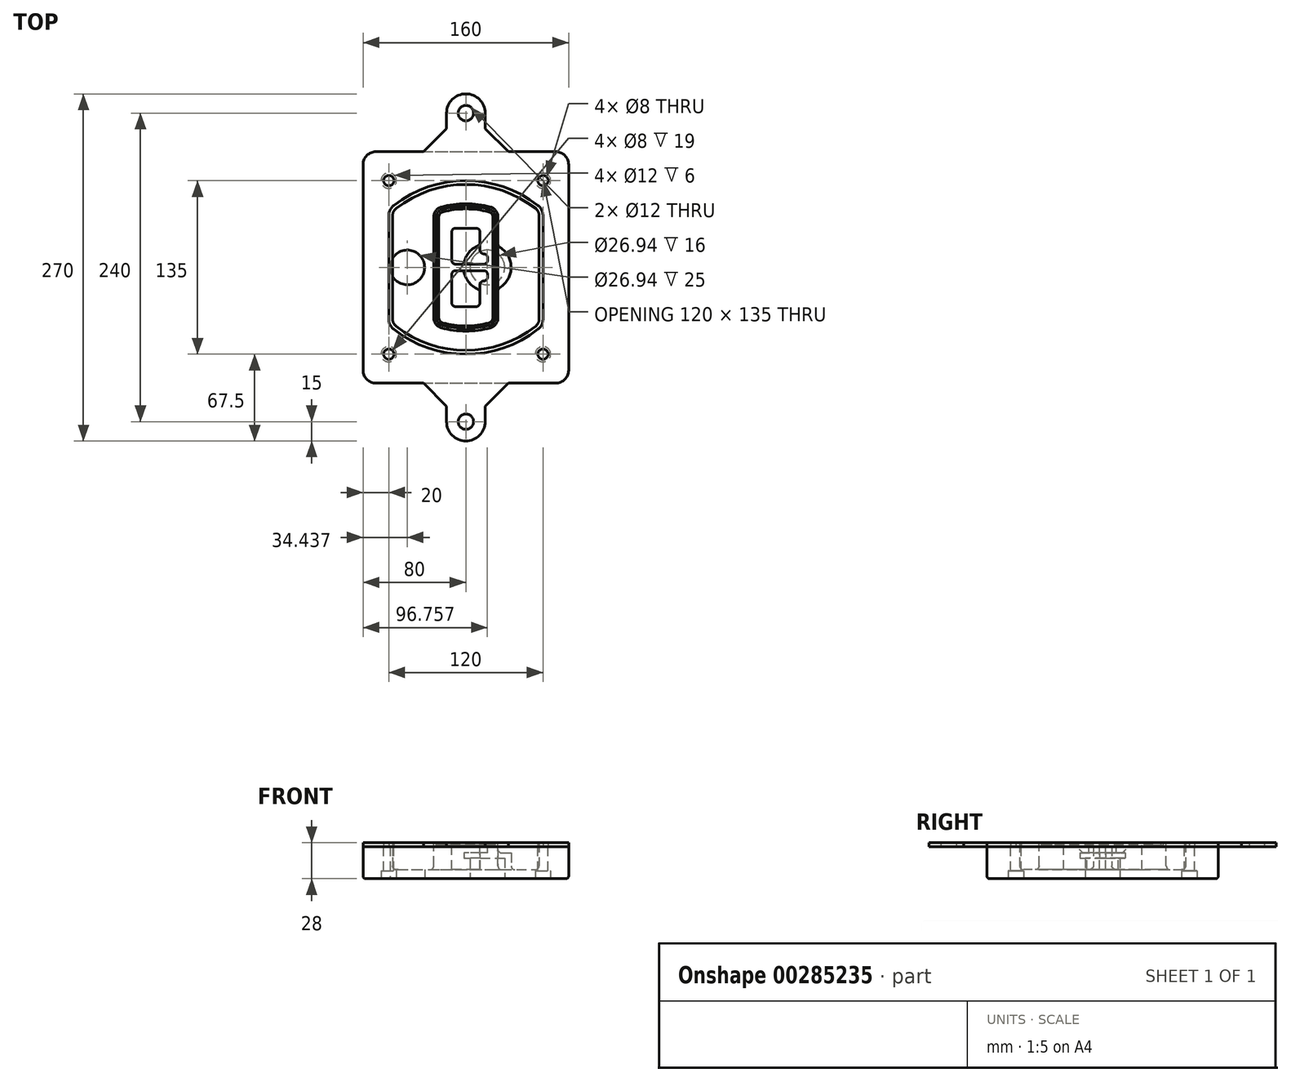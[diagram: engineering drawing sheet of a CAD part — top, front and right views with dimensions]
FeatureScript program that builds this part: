
annotation { "Feature Type Name" : "Feature", "Feature Type Description" : "" }
export const myFeature = defineFeature(function(context is Context, id is Id, definition is map)
    precondition{}
    {
        {
            var Q0;
            Q0=qCreatedBy(makeId("Top.planeOp"),FACE);
            var sketch = newSketch(context, id + "F0", { "sketchPlane" : qUnion([Q0])});
            skPoint(sketch, "E0.rect.middle", {"position": v(0, 0) * mm});
            skLineSegment(sketch, "E1.bottom", {"start": v(-70, -90) * mm, "end": v(70, -90) * mm});
            skLineSegment(sketch, "E1.top", {"start": v(-70, 90) * mm, "end": v(70, 90) * mm});
            skLineSegment(sketch, "E1.left", {"start": v(-80, -80) * mm, "end": v(-80, 80) * mm});
            skLineSegment(sketch, "E1.right", {"start": v(80, -80) * mm, "end": v(80, 80) * mm});
            skLineSegment(sketch, "E2", {"start": v(-80, 90) * mm, "end": v(80, -90) * mm, "construction": true});
            skLineSegment(sketch, "E3", {"start": v(80, 90) * mm, "end": v(-80, -90) * mm, "construction": true});
            skCircle(sketch, "E4", {"center": v(-60, 67.5) * mm, "radius": 4 * mm});
            skCircle(sketch, "E5", {"center": v(60, 67.5) * mm, "radius": 4 * mm});
            skCircle(sketch, "E6", {"center": v(60, -67.5) * mm, "radius": 4 * mm});
            skCircle(sketch, "E7", {"center": v(-60, -67.5) * mm, "radius": 4 * mm});
            skLineSegment(sketch, "E8", {"start": v(-60, 67.5) * mm, "end": v(60, 67.5) * mm, "construction": true});
            skLineSegment(sketch, "E9", {"start": v(60, 67.5) * mm, "end": v(60, -67.5) * mm, "construction": true});
            skLineSegment(sketch, "E10", {"start": v(60, -67.5) * mm, "end": v(-60, -67.5) * mm, "construction": true});
            skLineSegment(sketch, "E11", {"start": v(-60, -67.5) * mm, "end": v(-60, 67.5) * mm, "construction": true});
            skLineSegment(sketch, "E12", {"start": v(-60, 40.3) * mm, "end": v(-60, -40.3) * mm});
            skLineSegment(sketch, "E13", {"start": v(60, 40.3) * mm, "end": v(60, -40.3) * mm});
            skArc(sketch, "E14", {"start": v(56.15, 48.18) * mm, "mid": v(0, 67.5) * mm, "end": v(-56.15, 48.18) * mm});
            skArc(sketch, "E15", {"start": v(-56.15, -48.18) * mm, "mid": v(0, -67.5) * mm, "end": v(56.15, -48.18) * mm});
            skLineSegment(sketch, "E16", {"start": v(-60, 0) * mm, "end": v(60, 0) * mm, "construction": true});
            skPoint(sketch, "E17.visualSharp", {"position": v(-60, -45) * mm});
            skArc(sketch, "E17.filletArc", {"start": v(-60, -40.3) * mm, "mid": v(-58.99, -44.68) * mm, "end": v(-56.15, -48.18) * mm});
            skPoint(sketch, "E18.visualSharp", {"position": v(-60, 45) * mm});
            skArc(sketch, "E18.filletArc", {"start": v(-56.15, 48.18) * mm, "mid": v(-58.99, 44.68) * mm, "end": v(-60, 40.3) * mm});
            skPoint(sketch, "E19.visualSharp", {"position": v(60, 45) * mm});
            skArc(sketch, "E19.filletArc", {"start": v(60, 40.3) * mm, "mid": v(58.99, 44.68) * mm, "end": v(56.15, 48.18) * mm});
            skPoint(sketch, "E20.visualSharp", {"position": v(60, -45) * mm});
            skArc(sketch, "E20.filletArc", {"start": v(56.15, -48.18) * mm, "mid": v(58.99, -44.68) * mm, "end": v(60, -40.3) * mm});
            skPoint(sketch, "E21.visualSharp", {"position": v(-80, 90) * mm});
            skArc(sketch, "E21.filletArc", {"start": v(-70, 90) * mm, "mid": v(-77.07, 87.07) * mm, "end": v(-80, 80) * mm});
            skPoint(sketch, "E22.visualSharp", {"position": v(80, 90) * mm});
            skArc(sketch, "E22.filletArc", {"start": v(80, 80) * mm, "mid": v(77.07, 87.07) * mm, "end": v(70, 90) * mm});
            skPoint(sketch, "E23.visualSharp", {"position": v(80, -90) * mm});
            skArc(sketch, "E23.filletArc", {"start": v(70, -90) * mm, "mid": v(77.07, -87.07) * mm, "end": v(80, -80) * mm});
            skPoint(sketch, "E24.visualSharp", {"position": v(-80, -90) * mm});
            skArc(sketch, "E24.filletArc", {"start": v(-80, -80) * mm, "mid": v(-77.07, -87.07) * mm, "end": v(-70, -90) * mm});
            skArc(sketch, "E25.0", {"start": v(57, 40.3) * mm, "mid": v(56.3, 43.36) * mm, "end": v(54.3, 45.81) * mm});
            skLineSegment(sketch, "E25.1", {"start": v(57, 40.3) * mm, "end": v(57, -40.3) * mm});
            skArc(sketch, "E25.2", {"start": v(54.3, -45.81) * mm, "mid": v(56.3, -43.36) * mm, "end": v(57, -40.3) * mm});
            skArc(sketch, "E25.3", {"start": v(-54.3, -45.81) * mm, "mid": v(0, -64.5) * mm, "end": v(54.3, -45.81) * mm});
            skArc(sketch, "E25.4", {"start": v(-57, -40.3) * mm, "mid": v(-56.3, -43.36) * mm, "end": v(-54.3, -45.81) * mm});
            skArc(sketch, "E25.5", {"start": v(54.3, 45.81) * mm, "mid": v(0, 64.5) * mm, "end": v(-54.3, 45.81) * mm});
            skLineSegment(sketch, "E25.6", {"start": v(-57, 40.3) * mm, "end": v(-57, -40.3) * mm});
            skArc(sketch, "E25.7", {"start": v(-54.3, 45.81) * mm, "mid": v(-56.3, 43.36) * mm, "end": v(-57, 40.3) * mm});
            skArc(sketch, "E26.0", {"start": v(-58.62, 51.33) * mm, "mid": v(-62.58, 46.43) * mm, "end": v(-64, 40.3) * mm});
            skArc(sketch, "E26.1", {"start": v(58.62, 51.33) * mm, "mid": v(0, 71.5) * mm, "end": v(-58.62, 51.33) * mm});
            skArc(sketch, "E26.2", {"start": v(64, 40.3) * mm, "mid": v(62.58, 46.43) * mm, "end": v(58.62, 51.33) * mm});
            skLineSegment(sketch, "E26.3", {"start": v(64, 40.3) * mm, "end": v(64, -40.3) * mm});
            skArc(sketch, "E26.4", {"start": v(58.62, -51.33) * mm, "mid": v(62.58, -46.43) * mm, "end": v(64, -40.3) * mm});
            skLineSegment(sketch, "E26.5", {"start": v(-64, 40.3) * mm, "end": v(-64, -40.3) * mm});
            skArc(sketch, "E26.6", {"start": v(-58.62, -51.33) * mm, "mid": v(0, -71.5) * mm, "end": v(58.62, -51.33) * mm});
            skArc(sketch, "E26.7", {"start": v(-64, -40.3) * mm, "mid": v(-62.58, -46.43) * mm, "end": v(-58.62, -51.33) * mm});
            skSolve(sketch);
        }
        {
            var Q0;
            Q0=makeQuery(id+"F0.imprint","IMPRINT",FACE,{"disambiguationData":[TD([[makeQuery(id+"F0.imprint","IMPRINT",EDGE,{"derivedFrom":sQuery(id+"F0.wireOp",EDGE,"E1.bottom")}),1.0]])]});
            var Q1;
            Q1=makeQuery(id+"F0.imprint","IMPRINT",FACE,{"disambiguationData":[TD([[makeQuery(id+"F0.imprint","IMPRINT",EDGE,{"derivedFrom":sQuery(id+"F0.wireOp",EDGE,"E12")}),1.0]])]});
            var Q2;
            Q2=makeQuery(id+"F0.imprint","IMPRINT",FACE,{"disambiguationData":[TD([[makeQuery(id+"F0.imprint","IMPRINT",EDGE,{"derivedFrom":sQuery(id+"F0.wireOp",EDGE,"E25.0")}),1.0]])]});
            var Q3;
            Q3=makeQuery(id+"F0.imprint","IMPRINT",FACE,{"disambiguationData":[TD([[makeQuery(id+"F0.imprint","IMPRINT",EDGE,{"derivedFrom":sQuery(id+"F0.wireOp",EDGE,"E12")}),-1.0]])]});
            extrude(context, id + "F1", {"entities" : qUnion([Q0, Q1, Q2, Q3]), "oppositeDirection" : true, "depth" : 25 * mm});
        }
        {
            var Q0;
            Q0=makeQuery(id+"F0.imprint","IMPRINT",FACE,{"disambiguationData":[TD([[makeQuery(id+"F0.imprint","IMPRINT",EDGE,{"derivedFrom":sQuery(id+"F0.wireOp",EDGE,"E12")}),1.0]])]});
            extrude(context, id + "F2", {"entities" : qUnion([Q0]), "operationType" : NewBodyOperationType.ADD, "depth" : 3 * mm});
        }
        {
            var Q0;
            Q0=makeQuery(id+"F0.imprint","IMPRINT",FACE,{"disambiguationData":[TD([[makeQuery(id+"F0.imprint","IMPRINT",EDGE,{"derivedFrom":sQuery(id+"F0.wireOp",EDGE,"E25.0")}),1.0]])]});
            extrude(context, id + "F3", {"entities" : qUnion([Q0]), "operationType" : NewBodyOperationType.REMOVE, "oppositeDirection" : true, "depth" : 18 * mm});
        }
        {
            var Q0;
            Q0=makeQuery(id+"F2.opExtrude","CAP_FACE",FACE,{"disambiguationData":[OSD([sQuery(id+"F0.wireOp",EDGE,"E12"),sQuery(id+"F0.wireOp",EDGE,"E13"),sQuery(id+"F0.wireOp",EDGE,"E14"),sQuery(id+"F0.wireOp",EDGE,"E15"),sQuery(id+"F0.wireOp",EDGE,"E17.filletArc"),sQuery(id+"F0.wireOp",EDGE,"E18.filletArc"),sQuery(id+"F0.wireOp",EDGE,"E19.filletArc"),sQuery(id+"F0.wireOp",EDGE,"E20.filletArc"),sQuery(id+"F0.wireOp",EDGE,"E25.0"),sQuery(id+"F0.wireOp",EDGE,"E25.1"),sQuery(id+"F0.wireOp",EDGE,"E25.2"),sQuery(id+"F0.wireOp",EDGE,"E25.3"),sQuery(id+"F0.wireOp",EDGE,"E25.4"),sQuery(id+"F0.wireOp",EDGE,"E25.5"),sQuery(id+"F0.wireOp",EDGE,"E25.6"),sQuery(id+"F0.wireOp",EDGE,"E25.7")])],"isStart":false});
            var sketch = newSketch(context, id + "F4", { "sketchPlane" : qUnion([Q0])});
            skArc(sketch, "E27.0", {"start": v(-19.08, -46.97) * mm, "mid": v(0, -49.5) * mm, "end": v(19.08, -46.97) * mm});
            skArc(sketch, "E28.0", {"start": v(19.08, 46.97) * mm, "mid": v(0, 49.5) * mm, "end": v(-19.08, 46.97) * mm});
            skLineSegment(sketch, "E29", {"start": v(-25, 39.25) * mm, "end": v(-25, -39.25) * mm});
            skLineSegment(sketch, "E30", {"start": v(25, 39.25) * mm, "end": v(25, -39.25) * mm});
            skLineSegment(sketch, "E31", {"start": v(-25, 45.1) * mm, "end": v(25, 45.1) * mm, "construction": true});
            skLineSegment(sketch, "E32", {"start": v(-25, -45.1) * mm, "end": v(25, -45.1) * mm, "construction": true});
            skPoint(sketch, "E33.visualSharp", {"position": v(-25, 45.1) * mm});
            skArc(sketch, "E33.filletArc", {"start": v(-19.08, 46.97) * mm, "mid": v(-23.35, 44.11) * mm, "end": v(-25, 39.25) * mm});
            skPoint(sketch, "E34.visualSharp", {"position": v(25, 45.1) * mm});
            skArc(sketch, "E34.filletArc", {"start": v(25, 39.25) * mm, "mid": v(23.35, 44.11) * mm, "end": v(19.08, 46.97) * mm});
            skPoint(sketch, "E35.visualSharp", {"position": v(25, -45.1) * mm});
            skArc(sketch, "E35.filletArc", {"start": v(19.08, -46.97) * mm, "mid": v(23.35, -44.11) * mm, "end": v(25, -39.25) * mm});
            skPoint(sketch, "E36.visualSharp", {"position": v(-25, -45.1) * mm});
            skArc(sketch, "E36.filletArc", {"start": v(-25, -39.25) * mm, "mid": v(-23.35, -44.11) * mm, "end": v(-19.08, -46.97) * mm});
            skArc(sketch, "E37.0", {"start": v(54.3, 45.81) * mm, "mid": v(0, 64.5) * mm, "end": v(-54.3, 45.81) * mm});
            skArc(sketch, "E37.1", {"start": v(-54.3, 45.81) * mm, "mid": v(-56.3, 43.36) * mm, "end": v(-57, 40.3) * mm});
            skLineSegment(sketch, "E37.2", {"start": v(-57, 40.3) * mm, "end": v(-57, -40.3) * mm});
            skArc(sketch, "E37.3", {"start": v(-57, -40.3) * mm, "mid": v(-56.3, -43.36) * mm, "end": v(-54.3, -45.81) * mm});
            skArc(sketch, "E37.4", {"start": v(-54.3, -45.81) * mm, "mid": v(0, -64.5) * mm, "end": v(54.3, -45.81) * mm});
            skArc(sketch, "E37.5", {"start": v(54.3, -45.81) * mm, "mid": v(56.3, -43.36) * mm, "end": v(57, -40.3) * mm});
            skLineSegment(sketch, "E37.6", {"start": v(57, 40.3) * mm, "end": v(57, -40.3) * mm});
            skArc(sketch, "E37.7", {"start": v(57, 40.3) * mm, "mid": v(56.3, 43.36) * mm, "end": v(54.3, 45.81) * mm});
            skLineSegment(sketch, "E38.0", {"start": v(23, 39.25) * mm, "end": v(23, -39.25) * mm});
            skArc(sketch, "E38.1", {"start": v(18.56, -45.04) * mm, "mid": v(21.76, -42.9) * mm, "end": v(23, -39.25) * mm});
            skArc(sketch, "E38.2", {"start": v(-18.56, -45.04) * mm, "mid": v(0, -47.5) * mm, "end": v(18.56, -45.04) * mm});
            skArc(sketch, "E38.3", {"start": v(-23, -39.25) * mm, "mid": v(-21.76, -42.9) * mm, "end": v(-18.56, -45.04) * mm});
            skLineSegment(sketch, "E38.4", {"start": v(-23, 39.25) * mm, "end": v(-23, -39.25) * mm});
            skArc(sketch, "E38.5", {"start": v(23, 39.25) * mm, "mid": v(21.76, 42.9) * mm, "end": v(18.56, 45.04) * mm});
            skArc(sketch, "E38.6", {"start": v(-18.56, 45.04) * mm, "mid": v(-21.76, 42.9) * mm, "end": v(-23, 39.25) * mm});
            skArc(sketch, "E38.7", {"start": v(18.56, 45.04) * mm, "mid": v(0, 47.5) * mm, "end": v(-18.56, 45.04) * mm});
            skArc(sketch, "E39.0", {"start": v(21, 39.25) * mm, "mid": v(20.18, 41.68) * mm, "end": v(18.04, 43.1) * mm});
            skLineSegment(sketch, "E39.1", {"start": v(21, 39.25) * mm, "end": v(21, -39.25) * mm});
            skArc(sketch, "E39.2", {"start": v(18.04, -43.1) * mm, "mid": v(20.18, -41.68) * mm, "end": v(21, -39.25) * mm});
            skArc(sketch, "E39.3", {"start": v(-18.04, -43.1) * mm, "mid": v(0, -45.5) * mm, "end": v(18.04, -43.1) * mm});
            skArc(sketch, "E39.4", {"start": v(-21, -39.25) * mm, "mid": v(-20.18, -41.68) * mm, "end": v(-18.04, -43.1) * mm});
            skArc(sketch, "E39.5", {"start": v(18.04, 43.1) * mm, "mid": v(0, 45.5) * mm, "end": v(-18.04, 43.1) * mm});
            skLineSegment(sketch, "E39.6", {"start": v(-21, 39.25) * mm, "end": v(-21, -39.25) * mm});
            skArc(sketch, "E39.7", {"start": v(-18.04, 43.1) * mm, "mid": v(-20.18, 41.68) * mm, "end": v(-21, 39.25) * mm});
            skLineSegment(sketch, "E40", {"start": v(-25, 0) * mm, "end": v(25, 0) * mm, "construction": true});
            skLineSegment(sketch, "E41", {"start": v(-11, 5.5) * mm, "end": v(-11, 27.5) * mm});
            skLineSegment(sketch, "E42", {"start": v(-8, 30.5) * mm, "end": v(8, 30.5) * mm});
            skLineSegment(sketch, "E43", {"start": v(11, 27.5) * mm, "end": v(11, 13.5) * mm});
            skLineSegment(sketch, "E44", {"start": v(14, 10.5) * mm, "end": v(14, 10.5) * mm});
            skLineSegment(sketch, "E45", {"start": v(17, 7.5) * mm, "end": v(17, 5.5) * mm});
            skLineSegment(sketch, "E46", {"start": v(14, 2.5) * mm, "end": v(-8, 2.5) * mm});
            skPoint(sketch, "E47.visualSharp", {"position": v(-11, 30.5) * mm});
            skArc(sketch, "E47.filletArc", {"start": v(-8, 30.5) * mm, "mid": v(-10.12, 29.62) * mm, "end": v(-11, 27.5) * mm});
            skPoint(sketch, "E48.visualSharp", {"position": v(11, 30.5) * mm});
            skArc(sketch, "E48.filletArc", {"start": v(11, 27.5) * mm, "mid": v(10.12, 29.62) * mm, "end": v(8, 30.5) * mm});
            skPoint(sketch, "E49.visualSharp", {"position": v(11, 10.5) * mm});
            skArc(sketch, "E49.filletArc", {"start": v(11, 13.5) * mm, "mid": v(11.88, 11.38) * mm, "end": v(14, 10.5) * mm});
            skPoint(sketch, "E50.visualSharp", {"position": v(17, 10.5) * mm});
            skArc(sketch, "E50.filletArc", {"start": v(17, 7.5) * mm, "mid": v(16.12, 9.62) * mm, "end": v(14, 10.5) * mm});
            skPoint(sketch, "E51.visualSharp", {"position": v(17, 2.5) * mm});
            skArc(sketch, "E51.filletArc", {"start": v(14, 2.5) * mm, "mid": v(16.12, 3.38) * mm, "end": v(17, 5.5) * mm});
            skPoint(sketch, "E52.visualSharp", {"position": v(-11, 2.5) * mm});
            skArc(sketch, "E52.filletArc", {"start": v(-11, 5.5) * mm, "mid": v(-10.12, 3.38) * mm, "end": v(-8, 2.5) * mm});
            skLineSegment(sketch, "E53.0.MirrorCS", {"start": v(14, -2.5) * mm, "end": v(-8, -2.5) * mm});
            skArc(sketch, "E54.0.MirrorCS", {"start": v(-11, -5.5) * mm, "mid": v(-10.12, -3.38) * mm, "end": v(-8, -2.5) * mm});
            skLineSegment(sketch, "E55.0.MirrorCS", {"start": v(-11, -5.5) * mm, "end": v(-11, -27.5) * mm});
            skArc(sketch, "E56.0.MirrorCS", {"start": v(-8, -30.5) * mm, "mid": v(-10.12, -29.62) * mm, "end": v(-11, -27.5) * mm});
            skLineSegment(sketch, "E57.0.MirrorCS", {"start": v(-8, -30.5) * mm, "end": v(8, -30.5) * mm});
            skArc(sketch, "E58.0.MirrorCS", {"start": v(11, -27.5) * mm, "mid": v(10.12, -29.62) * mm, "end": v(8, -30.5) * mm});
            skLineSegment(sketch, "E59.0.MirrorCS", {"start": v(11, -27.5) * mm, "end": v(11, -13.5) * mm});
            skArc(sketch, "E60.0.MirrorCS", {"start": v(11, -13.5) * mm, "mid": v(11.88, -11.38) * mm, "end": v(14, -10.5) * mm});
            skArc(sketch, "E61.0.MirrorCS", {"start": v(17, -7.5) * mm, "mid": v(16.12, -9.62) * mm, "end": v(14, -10.5) * mm});
            skLineSegment(sketch, "E62.0.MirrorCS", {"start": v(17, -7.5) * mm, "end": v(17, -5.5) * mm});
            skArc(sketch, "E63.0.MirrorCS", {"start": v(14, -2.5) * mm, "mid": v(16.12, -3.38) * mm, "end": v(17, -5.5) * mm});
            skSolve(sketch);
        }
        {
            var Q0;
            Q0=makeQuery(id+"F4.imprint","IMPRINT",FACE,{"disambiguationData":[TD([[makeQuery(id+"F4.imprint","IMPRINT",EDGE,{"derivedFrom":sQuery(id+"F4.wireOp",EDGE,"E27.0")}),1.0]])]});
            var Q1;
            Q1=makeQuery(id+"F4.imprint","IMPRINT",FACE,{"disambiguationData":[TD([[makeQuery(id+"F4.imprint","IMPRINT",EDGE,{"derivedFrom":sQuery(id+"F4.wireOp",EDGE,"E38.0")}),-1.0]])]});
            var Q2;
            Q2=makeQuery(id+"F4.imprint","IMPRINT",FACE,{"disambiguationData":[TD([[makeQuery(id+"F4.imprint","IMPRINT",EDGE,{"derivedFrom":sQuery(id+"F4.wireOp",EDGE,"E39.0")}),1.0]])]});
            extrude(context, id + "F5", {"entities" : qUnion([Q0, Q1, Q2]), "operationType" : NewBodyOperationType.ADD, "endBound" : BoundingType.UP_TO_NEXT, "oppositeDirection" : true, "depth" : 25 * mm});
        }
        {
            var Q0;
            Q0=makeQuery(id+"F4.imprint","IMPRINT",FACE,{"disambiguationData":[TD([[makeQuery(id+"F4.imprint","IMPRINT",EDGE,{"derivedFrom":sQuery(id+"F4.wireOp",EDGE,"E38.0")}),-1.0]])]});
            extrude(context, id + "F6", {"entities" : qUnion([Q0]), "operationType" : NewBodyOperationType.REMOVE, "oppositeDirection" : true, "depth" : 2 * mm});
        }
        {
            var Q0;
            Q0=makeQuery(id+"F1.opExtrude","CAP_FACE",FACE,{"disambiguationData":[OSD([sQuery(id+"F0.wireOp",EDGE,"E1.bottom"),sQuery(id+"F0.wireOp",EDGE,"E1.top"),sQuery(id+"F0.wireOp",EDGE,"E1.left"),sQuery(id+"F0.wireOp",EDGE,"E1.right"),sQuery(id+"F0.wireOp",EDGE,"E4"),sQuery(id+"F0.wireOp",EDGE,"E5"),sQuery(id+"F0.wireOp",EDGE,"E6"),sQuery(id+"F0.wireOp",EDGE,"E7"),sQuery(id+"F0.wireOp",EDGE,"E21.filletArc"),sQuery(id+"F0.wireOp",EDGE,"E22.filletArc"),sQuery(id+"F0.wireOp",EDGE,"E23.filletArc"),sQuery(id+"F0.wireOp",EDGE,"E24.filletArc")])],"isStart":false});
            var sketch = newSketch(context, id + "F7", { "sketchPlane" : qUnion([Q0])});
            skCircle(sketch, "E64", {"center": v(16.76, 0) * mm, "radius": 13.47 * mm});
            skCircle(sketch, "E65", {"center": v(-45.56, 0) * mm, "radius": 13.47 * mm});
            skLineSegment(sketch, "E66", {"start": v(80, 0) * mm, "end": v(-80, 0) * mm});
            skCircle(sketch, "E67", {"center": v(16.76, 0) * mm, "radius": 18.47 * mm});
            skCircle(sketch, "E68", {"center": v(60, -67.5) * mm, "radius": 6 * mm});
            skCircle(sketch, "E69", {"center": v(-60, -67.5) * mm, "radius": 6 * mm});
            skCircle(sketch, "E70", {"center": v(-60, 67.5) * mm, "radius": 6 * mm});
            skCircle(sketch, "E71", {"center": v(60, 67.5) * mm, "radius": 6 * mm});
            skSolve(sketch);
        }
        {
            var Q0;
            {var subQ1=sQuery(id+"F7.wireOp",EDGE,"E66");var subQ4=sQuery(id+"F7.wireOp",EDGE,"E64");var subQ6=makeQuery(id+"F7.imprint","INTERSECT",VERTEX,{"disambiguationData":[OD(0.0)],"derivedFrom":[subQ4,subQ1]});Q0=makeQuery(id+"F7.imprint","IMPRINT",FACE,{"disambiguationData":[TD([[makeQuery(id+"F7.imprint","IMPRINT",EDGE,{"disambiguationData":[TD([[subQ6,-1.0]])],"derivedFrom":subQ4}),-1.0]])]});}
            var Q1;
            {var subQ0=sQuery(id+"F7.wireOp",EDGE,"E66");var subQ1=sQuery(id+"F7.wireOp",EDGE,"E64");var subQ3=makeQuery(id+"F7.imprint","INTERSECT",VERTEX,{"disambiguationData":[OD(0.0)],"derivedFrom":[subQ1,subQ0]});Q1=makeQuery(id+"F7.imprint","IMPRINT",FACE,{"disambiguationData":[TD([[makeQuery(id+"F7.imprint","IMPRINT",EDGE,{"disambiguationData":[TD([[subQ3,-1.0]])],"derivedFrom":subQ1}),1.0]])]});}
            var Q2;
            {var subQ0=sQuery(id+"F7.wireOp",EDGE,"E66");var subQ1=sQuery(id+"F7.wireOp",EDGE,"E64");var subQ3=makeQuery(id+"F7.imprint","INTERSECT",VERTEX,{"disambiguationData":[OD(0.0)],"derivedFrom":[subQ1,subQ0]});Q2=makeQuery(id+"F7.imprint","IMPRINT",FACE,{"disambiguationData":[TD([[makeQuery(id+"F7.imprint","IMPRINT",EDGE,{"disambiguationData":[TD([[subQ3,1.0]])],"derivedFrom":subQ1}),1.0]])]});}
            var Q3;
            {var subQ1=sQuery(id+"F7.wireOp",EDGE,"E66");var subQ4=sQuery(id+"F7.wireOp",EDGE,"E64");var subQ6=makeQuery(id+"F7.imprint","INTERSECT",VERTEX,{"disambiguationData":[OD(0.0)],"derivedFrom":[subQ4,subQ1]});Q3=makeQuery(id+"F7.imprint","IMPRINT",FACE,{"disambiguationData":[TD([[makeQuery(id+"F7.imprint","IMPRINT",EDGE,{"disambiguationData":[TD([[subQ6,1.0]])],"derivedFrom":subQ4}),-1.0]])]});}
            extrude(context, id + "F8", {"entities" : qUnion([Q0, Q1, Q2, Q3]), "operationType" : NewBodyOperationType.ADD, "oppositeDirection" : true, "depth" : 20 * mm});
        }
        {
            var Q0;
            {var subQ0=sQuery(id+"F7.wireOp",EDGE,"E66");var subQ1=sQuery(id+"F7.wireOp",EDGE,"E64");var subQ3=makeQuery(id+"F7.imprint","INTERSECT",VERTEX,{"disambiguationData":[OD(0.0)],"derivedFrom":[subQ1,subQ0]});Q0=makeQuery(id+"F7.imprint","IMPRINT",FACE,{"disambiguationData":[TD([[makeQuery(id+"F7.imprint","IMPRINT",EDGE,{"disambiguationData":[TD([[subQ3,-1.0]])],"derivedFrom":subQ1}),1.0]])]});}
            var Q1;
            {var subQ0=sQuery(id+"F7.wireOp",EDGE,"E66");var subQ1=sQuery(id+"F7.wireOp",EDGE,"E64");var subQ3=makeQuery(id+"F7.imprint","INTERSECT",VERTEX,{"disambiguationData":[OD(0.0)],"derivedFrom":[subQ1,subQ0]});Q1=makeQuery(id+"F7.imprint","IMPRINT",FACE,{"disambiguationData":[TD([[makeQuery(id+"F7.imprint","IMPRINT",EDGE,{"disambiguationData":[TD([[subQ3,1.0]])],"derivedFrom":subQ1}),1.0]])]});}
            extrude(context, id + "F9", {"entities" : qUnion([Q0, Q1]), "operationType" : NewBodyOperationType.REMOVE, "oppositeDirection" : true, "depth" : 16 * mm});
        }
        {
            var Q0;
            {var subQ0=sQuery(id+"F7.wireOp",EDGE,"E66");var subQ1=sQuery(id+"F7.wireOp",EDGE,"E65");var subQ3=makeQuery(id+"F7.imprint","INTERSECT",VERTEX,{"disambiguationData":[OD(0.0)],"derivedFrom":[subQ1,subQ0]});Q0=makeQuery(id+"F7.imprint","IMPRINT",FACE,{"disambiguationData":[TD([[makeQuery(id+"F7.imprint","IMPRINT",EDGE,{"disambiguationData":[TD([[subQ3,-1.0]])],"derivedFrom":subQ1}),1.0]])]});}
            var Q1;
            {var subQ0=sQuery(id+"F7.wireOp",EDGE,"E66");var subQ1=sQuery(id+"F7.wireOp",EDGE,"E65");var subQ3=makeQuery(id+"F7.imprint","INTERSECT",VERTEX,{"disambiguationData":[OD(0.0)],"derivedFrom":[subQ1,subQ0]});Q1=makeQuery(id+"F7.imprint","IMPRINT",FACE,{"disambiguationData":[TD([[makeQuery(id+"F7.imprint","IMPRINT",EDGE,{"disambiguationData":[TD([[subQ3,1.0]])],"derivedFrom":subQ1}),1.0]])]});}
            extrude(context, id + "F10", {"entities" : qUnion([Q0, Q1]), "operationType" : NewBodyOperationType.REMOVE, "oppositeDirection" : true, "depth" : 25 * mm});
        }
        {
            var Q0;
            Q0=makeQuery(id+"F7.imprint","IMPRINT",FACE,{"disambiguationData":[TD([[makeQuery(id+"F7.imprint","IMPRINT",EDGE,{"derivedFrom":sQuery(id+"F7.wireOp",EDGE,"E68")}),1.0]])]});
            var Q1;
            Q1=makeQuery(id+"F7.imprint","IMPRINT",FACE,{"disambiguationData":[TD([[makeQuery(id+"F7.imprint","IMPRINT",EDGE,{"derivedFrom":makeQuery(id+"F1.opExtrude","CAP_EDGE",EDGE,{"disambiguationData":[OSD([sQuery(id+"F0.wireOp",EDGE,"E5")])],"isStart":false})}),-1.0]])]});
            var Q2;
            Q2=makeQuery(id+"F7.imprint","IMPRINT",FACE,{"disambiguationData":[TD([[makeQuery(id+"F7.imprint","IMPRINT",EDGE,{"derivedFrom":sQuery(id+"F7.wireOp",EDGE,"E69")}),1.0]])]});
            var Q3;
            Q3=makeQuery(id+"F7.imprint","IMPRINT",FACE,{"disambiguationData":[TD([[makeQuery(id+"F7.imprint","IMPRINT",EDGE,{"derivedFrom":makeQuery(id+"F1.opExtrude","CAP_EDGE",EDGE,{"disambiguationData":[OSD([sQuery(id+"F0.wireOp",EDGE,"E4")])],"isStart":false})}),-1.0]])]});
            var Q4;
            Q4=makeQuery(id+"F7.imprint","IMPRINT",FACE,{"disambiguationData":[TD([[makeQuery(id+"F7.imprint","IMPRINT",EDGE,{"derivedFrom":sQuery(id+"F7.wireOp",EDGE,"E70")}),1.0]])]});
            var Q5;
            Q5=makeQuery(id+"F7.imprint","IMPRINT",FACE,{"disambiguationData":[TD([[makeQuery(id+"F7.imprint","IMPRINT",EDGE,{"derivedFrom":makeQuery(id+"F1.opExtrude","CAP_EDGE",EDGE,{"disambiguationData":[OSD([sQuery(id+"F0.wireOp",EDGE,"E7")])],"isStart":false})}),-1.0]])]});
            var Q6;
            Q6=makeQuery(id+"F7.imprint","IMPRINT",FACE,{"disambiguationData":[TD([[makeQuery(id+"F7.imprint","IMPRINT",EDGE,{"derivedFrom":sQuery(id+"F7.wireOp",EDGE,"E71")}),1.0]])]});
            var Q7;
            Q7=makeQuery(id+"F7.imprint","IMPRINT",FACE,{"disambiguationData":[TD([[makeQuery(id+"F7.imprint","IMPRINT",EDGE,{"derivedFrom":makeQuery(id+"F1.opExtrude","CAP_EDGE",EDGE,{"disambiguationData":[OSD([sQuery(id+"F0.wireOp",EDGE,"E6")])],"isStart":false})}),-1.0]])]});
            extrude(context, id + "F11", {"entities" : qUnion([Q0, Q1, Q2, Q3, Q4, Q5, Q6, Q7]), "operationType" : NewBodyOperationType.REMOVE, "oppositeDirection" : true, "depth" : 6 * mm});
        }
        {
            var Q0;
            Q0=makeQuery(id+"F9.boolean.opBoolean","COPY",FACE,{"derivedFrom":makeQuery(id+"F9.opExtrude","CAP_FACE",FACE,{"disambiguationData":[OSD([sQuery(id+"F7.wireOp",EDGE,"E64")])],"isStart":false})});
            var sketch = newSketch(context, id + "F12", { "sketchPlane" : qUnion([Q0])});
            skArc(sketch, "E72.0", {"start": v(11, 17.55) * mm, "mid": v(2.57, 11.82) * mm, "end": v(-1.54, 2.5) * mm});
            skArc(sketch, "E72.1", {"start": v(-1.54, -2.5) * mm, "mid": v(2.57, -11.82) * mm, "end": v(11, -17.55) * mm});
            skLineSegment(sketch, "E73", {"start": v(-1.54, -2.5) * mm, "end": v(14, -2.5) * mm});
            skLineSegment(sketch, "E74.0", {"start": v(14, 2.5) * mm, "end": v(-1.54, 2.5) * mm});
            skArc(sketch, "E74.1", {"start": v(14, 2.5) * mm, "mid": v(16.12, 3.38) * mm, "end": v(17, 5.5) * mm});
            skLineSegment(sketch, "E74.2", {"start": v(17, 7.5) * mm, "end": v(17, 5.5) * mm});
            skArc(sketch, "E74.3", {"start": v(17, 7.5) * mm, "mid": v(16.12, 9.62) * mm, "end": v(14, 10.5) * mm});
            skArc(sketch, "E74.4", {"start": v(11, 13.5) * mm, "mid": v(11.88, 11.38) * mm, "end": v(14, 10.5) * mm});
            skLineSegment(sketch, "E74.5", {"start": v(11, 17.55) * mm, "end": v(11, 13.5) * mm});
            skLineSegment(sketch, "E74.7", {"start": v(14, -2.5) * mm, "end": v(-1.54, -2.5) * mm});
            skArc(sketch, "E74.8", {"start": v(14, -2.5) * mm, "mid": v(16.12, -3.38) * mm, "end": v(17, -5.5) * mm});
            skLineSegment(sketch, "E74.9", {"start": v(17, -7.5) * mm, "end": v(17, -5.5) * mm});
            skArc(sketch, "E74.10", {"start": v(17, -7.5) * mm, "mid": v(16.12, -9.62) * mm, "end": v(14, -10.5) * mm});
            skArc(sketch, "E74.11", {"start": v(11, -13.5) * mm, "mid": v(11.88, -11.38) * mm, "end": v(14, -10.5) * mm});
            skLineSegment(sketch, "E74.12", {"start": v(11, -17.55) * mm, "end": v(11, -13.5) * mm});
            skPoint(sketch, "E75.orphan", {"position": v(11, -27.5) * mm});
            skPoint(sketch, "E76.orphan", {"position": v(-8, -2.5) * mm});
            skPoint(sketch, "E77.orphan", {"position": v(-8, 2.5) * mm});
            skPoint(sketch, "E78.orphan", {"position": v(11, 27.5) * mm});
            skSolve(sketch);
        }
        {
            var Q0;
            {var subQ7=sQuery(id+"F12.wireOp",EDGE,"E72.0");var subQ14=sQuery(id+"F12.wireOp",EDGE,"E72.1");var subQ16=sQuery(id+"F12.wireOp",EDGE,"E74.1");var subQ18=sQuery(id+"F12.wireOp",EDGE,"E74.8");Q0=qUnion([makeQuery(id+"F12.imprint","IMPRINT",FACE,{"disambiguationData":[TD([[makeQuery(id+"F12.imprint","IMPRINT",EDGE,{"derivedFrom":subQ7}),1.0]])]}),makeQuery(id+"F12.imprint","IMPRINT",FACE,{"disambiguationData":[TD([[makeQuery(id+"F12.imprint","IMPRINT",EDGE,{"derivedFrom":subQ14}),1.0]])]}),makeQuery(id+"F12.imprint","IMPRINT",FACE,{"disambiguationData":[TD([[makeQuery(id+"F12.imprint","IMPRINT",EDGE,{"derivedFrom":subQ16}),1.0]])]}),makeQuery(id+"F12.imprint","IMPRINT",FACE,{"disambiguationData":[TD([[makeQuery(id+"F12.imprint","IMPRINT",EDGE,{"derivedFrom":subQ18}),-1.0]])]})]);}
            var Q1;
            Q1=makeQuery(id+"F5.boolean.opBoolean","SPLIT",FACE,{"disambiguationData":[TD([makeQuery(id+"F5.opExtrude","SWEPT_FACE",FACE,{"disambiguationData":[OSD([sQuery(id+"F4.wireOp",EDGE,"E41")])]})])],"derivedFrom":makeQuery(id+"F3.boolean.opBoolean","COPY",FACE,{"derivedFrom":makeQuery(id+"F3.opExtrude","CAP_FACE",FACE,{"disambiguationData":[OSD([sQuery(id+"F0.wireOp",EDGE,"E25.0"),sQuery(id+"F0.wireOp",EDGE,"E25.1"),sQuery(id+"F0.wireOp",EDGE,"E25.2"),sQuery(id+"F0.wireOp",EDGE,"E25.3"),sQuery(id+"F0.wireOp",EDGE,"E25.4"),sQuery(id+"F0.wireOp",EDGE,"E25.5"),sQuery(id+"F0.wireOp",EDGE,"E25.6"),sQuery(id+"F0.wireOp",EDGE,"E25.7")])],"isStart":false})})});
            extrude(context, id + "F13", {"entities" : qUnion([Q0]), "operationType" : NewBodyOperationType.REMOVE, "endBound" : BoundingType.UP_TO_SURFACE, "endBoundEntityFace" : qUnion([Q1]), "depth" : 25 * mm});
        }
        {
            var Q0;
            Q0=makeQuery(id+"F3.boolean.opBoolean","COPY",EDGE,{"derivedFrom":makeQuery(id+"F3.opExtrude","CAP_EDGE",EDGE,{"disambiguationData":[OSD([sQuery(id+"F0.wireOp",EDGE,"E25.6")])],"isStart":false})});
            var Q1;
            Q1=makeQuery(id+"F8.boolean.opBoolean","INTERSECT",EDGE,{"derivedFrom":[makeQuery(id+"F5.opExtrude","SWEPT_FACE",FACE,{"disambiguationData":[OSD([sQuery(id+"F4.wireOp",EDGE,"E30")])]}),makeQuery(id+"F8.opExtrude","CAP_FACE",FACE,{"disambiguationData":[OSD([sQuery(id+"F7.wireOp",EDGE,"E67")])],"isStart":false})]});
            var Q2;
            Q2=makeQuery(id+"F8.boolean.opBoolean","INTERSECT",EDGE,{"disambiguationData":[OD(1.0)],"derivedFrom":[makeQuery(id+"F5.opExtrude","SWEPT_FACE",FACE,{"disambiguationData":[OSD([sQuery(id+"F4.wireOp",EDGE,"E30")])]}),makeQuery(id+"F8.opExtrude","SWEPT_FACE",FACE,{"disambiguationData":[OSD([sQuery(id+"F7.wireOp",EDGE,"E67")])]})]});
            var Q3;
            {var subQ0=sQuery(id+"F4.wireOp",EDGE,"E30");Q3=makeQuery(id+"F8.boolean.opBoolean","SPLIT",EDGE,{"disambiguationData":[TD([makeQuery(id+"F5.opExtrude","SWEPT_FACE",FACE,{"disambiguationData":[OSD([sQuery(id+"F4.wireOp",EDGE,"E35.filletArc")])]})])],"derivedFrom":makeQuery(id+"F5.opExtrude","CAP_EDGE",EDGE,{"disambiguationData":[OSD([subQ0])],"isStart":false})});}
            var Q4;
            {var subQ0=sQuery(id+"F0.wireOp",EDGE,"E25.7");var subQ1=sQuery(id+"F0.wireOp",EDGE,"E25.1");var subQ2=sQuery(id+"F0.wireOp",EDGE,"E25.6");var subQ3=sQuery(id+"F0.wireOp",EDGE,"E25.5");var subQ4=sQuery(id+"F0.wireOp",EDGE,"E25.4");var subQ5=sQuery(id+"F0.wireOp",EDGE,"E25.0");var subQ6=sQuery(id+"F0.wireOp",EDGE,"E25.2");var subQ7=sQuery(id+"F0.wireOp",EDGE,"E25.3");Q4=makeQuery(id+"F8.boolean.opBoolean","INTERSECT",EDGE,{"derivedFrom":[makeQuery(id+"F5.boolean.opBoolean","SPLIT",FACE,{"disambiguationData":[TD([makeQuery(id+"F2.opExtrude","SWEPT_FACE",FACE,{"disambiguationData":[OSD([subQ5])]})])],"derivedFrom":makeQuery(id+"F3.boolean.opBoolean","COPY",FACE,{"derivedFrom":makeQuery(id+"F3.opExtrude","CAP_FACE",FACE,{"disambiguationData":[OSD([subQ5,subQ1,subQ6,subQ7,subQ4,subQ3,subQ2,subQ0])],"isStart":false})})}),makeQuery(id+"F8.opExtrude","SWEPT_FACE",FACE,{"disambiguationData":[OSD([sQuery(id+"F7.wireOp",EDGE,"E67")])]})]});}
            var Q5;
            Q5=makeQuery(id+"F8.boolean.opBoolean","INTERSECT",EDGE,{"disambiguationData":[OD(0.0)],"derivedFrom":[makeQuery(id+"F5.opExtrude","SWEPT_FACE",FACE,{"disambiguationData":[OSD([sQuery(id+"F4.wireOp",EDGE,"E30")])]}),makeQuery(id+"F8.opExtrude","SWEPT_FACE",FACE,{"disambiguationData":[OSD([sQuery(id+"F7.wireOp",EDGE,"E67")])]})]});
            fillet(context, id + "F14", {"entities" : qUnion([Q0, Q1, Q2, Q3, Q4, Q5]), "radius" : 3 * mm, "tangentPropagation" : true, "allowEdgeOverflow" : false});
        }
        {
            var Q0;
            Q0=makeQuery(id+"F1.opExtrude","CAP_EDGE",EDGE,{"disambiguationData":[OSD([sQuery(id+"F0.wireOp",EDGE,"E1.bottom")])],"isStart":false});
            fillet(context, id + "F15", {"entities" : qUnion([Q0]), "radius" : 2 * mm, "tangentPropagation" : true, "allowEdgeOverflow" : false});
        }
        {
            var Q0;
            {var subQ0=sQuery(id+"F0.wireOp",EDGE,"E21.filletArc");var subQ1=sQuery(id+"F0.wireOp",EDGE,"E7");var subQ2=sQuery(id+"F0.wireOp",EDGE,"E6");var subQ3=sQuery(id+"F0.wireOp",EDGE,"E5");var subQ4=sQuery(id+"F0.wireOp",EDGE,"E4");var subQ5=sQuery(id+"F0.wireOp",EDGE,"E22.filletArc");var subQ6=sQuery(id+"F0.wireOp",EDGE,"E1.bottom");var subQ7=sQuery(id+"F0.wireOp",EDGE,"E1.right");var subQ8=sQuery(id+"F0.wireOp",EDGE,"E1.top");var subQ9=sQuery(id+"F0.wireOp",EDGE,"E1.left");var subQ10=sQuery(id+"F0.wireOp",EDGE,"E23.filletArc");var subQ11=sQuery(id+"F0.wireOp",EDGE,"E24.filletArc");Q0=makeQuery(id+"F2.boolean.opBoolean","SPLIT",FACE,{"disambiguationData":[TD([makeQuery(id+"F1.opExtrude","SWEPT_FACE",FACE,{"disambiguationData":[OSD([subQ6])]})])],"derivedFrom":makeQuery(id+"F1.opExtrude","CAP_FACE",FACE,{"disambiguationData":[OSD([subQ6,subQ8,subQ9,subQ7,subQ4,subQ3,subQ2,subQ1,subQ0,subQ5,subQ10,subQ11])],"isStart":true})});}
            var sketch = newSketch(context, id + "F16", { "sketchPlane" : qUnion([Q0])});
            skLineSegment(sketch, "E79.0.0", {"start": v(70, 90) * mm, "end": v(-70, 90) * mm});
            skArc(sketch, "E79.0.1", {"start": v(-70, 90) * mm, "mid": v(-77.07, 87.07) * mm, "end": v(-80, 80) * mm});
            skLineSegment(sketch, "E79.0.2", {"start": v(-80, 80) * mm, "end": v(-80, -80) * mm});
            skArc(sketch, "E79.0.3", {"start": v(-80, -80) * mm, "mid": v(-77.07, -87.07) * mm, "end": v(-70, -90) * mm});
            skLineSegment(sketch, "E79.0.4", {"start": v(-70, -90) * mm, "end": v(70, -90) * mm});
            skArc(sketch, "E79.0.5", {"start": v(70, -90) * mm, "mid": v(77.07, -87.07) * mm, "end": v(80, -80) * mm});
            skLineSegment(sketch, "E79.0.6", {"start": v(80, -80) * mm, "end": v(80, 80) * mm});
            skArc(sketch, "E79.0.7", {"start": v(80, 80) * mm, "mid": v(77.07, 87.07) * mm, "end": v(70, 90) * mm});
            skCircle(sketch, "E80.0", {"center": v(-60, 67.5) * mm, "radius": 4 * mm});
            skCircle(sketch, "E81.0", {"center": v(60, 67.5) * mm, "radius": 4 * mm});
            skCircle(sketch, "E82.0", {"center": v(-60, -67.5) * mm, "radius": 4 * mm});
            skCircle(sketch, "E83.0", {"center": v(60, -67.5) * mm, "radius": 4 * mm});
            skLineSegment(sketch, "E84.0.0", {"start": v(60, -40.3) * mm, "end": v(60, 40.3) * mm});
            skArc(sketch, "E84.0.1", {"start": v(60, 40.3) * mm, "mid": v(58.99, 44.68) * mm, "end": v(56.15, 48.18) * mm});
            skArc(sketch, "E84.0.2", {"start": v(56.15, 48.18) * mm, "mid": v(0, 67.5) * mm, "end": v(-56.15, 48.18) * mm});
            skArc(sketch, "E84.0.3", {"start": v(-56.15, 48.18) * mm, "mid": v(-58.99, 44.68) * mm, "end": v(-60, 40.3) * mm});
            skLineSegment(sketch, "E84.0.4", {"start": v(-60, 40.3) * mm, "end": v(-60, -40.3) * mm});
            skArc(sketch, "E84.0.5", {"start": v(-60, -40.3) * mm, "mid": v(-58.99, -44.68) * mm, "end": v(-56.15, -48.18) * mm});
            skArc(sketch, "E84.0.6", {"start": v(-56.15, -48.18) * mm, "mid": v(0, -67.5) * mm, "end": v(56.15, -48.18) * mm});
            skArc(sketch, "E84.0.7", {"start": v(56.15, -48.18) * mm, "mid": v(58.99, -44.68) * mm, "end": v(60, -40.3) * mm});
            skLineSegment(sketch, "E85", {"start": v(-33, 90) * mm, "end": v(-15, 108) * mm});
            skLineSegment(sketch, "E86", {"start": v(-15, 108) * mm, "end": v(-15, 120) * mm});
            skLineSegment(sketch, "E87", {"start": v(15, 120) * mm, "end": v(15, 108) * mm});
            skLineSegment(sketch, "E88", {"start": v(15, 108) * mm, "end": v(33, 90) * mm});
            skArc(sketch, "E89", {"start": v(15, 120) * mm, "mid": v(0, 135) * mm, "end": v(-15, 120) * mm});
            skCircle(sketch, "E90", {"center": v(0, 120) * mm, "radius": 6 * mm});
            skLineSegment(sketch, "E91", {"start": v(0, 120) * mm, "end": v(0, 90) * mm, "construction": true});
            skLineSegment(sketch, "E92", {"start": v(-80, 0) * mm, "end": v(80, 0) * mm, "construction": true});
            skLineSegment(sketch, "E93.MirrorCS", {"start": v(-33, -90) * mm, "end": v(-15, -108) * mm});
            skLineSegment(sketch, "E94.MirrorCS", {"start": v(0, -120) * mm, "end": v(0, -90) * mm, "construction": true});
            skLineSegment(sketch, "E95.MirrorCS", {"start": v(-15, -108) * mm, "end": v(-15, -120) * mm});
            skArc(sketch, "E96.MirrorCS", {"start": v(15, -120) * mm, "mid": v(0, -135) * mm, "end": v(-15, -120) * mm});
            skCircle(sketch, "E97.MirrorC", {"center": v(0, -120) * mm, "radius": 6 * mm});
            skLineSegment(sketch, "E98.MirrorCS", {"start": v(15, -108) * mm, "end": v(33, -90) * mm});
            skLineSegment(sketch, "E99.MirrorCS", {"start": v(15, -120) * mm, "end": v(15, -108) * mm});
            skSolve(sketch);
        }
        {
            var Q0;
            {var subQ1=sQuery(id+"F16.wireOp",EDGE,"E79.0.1");Q0=makeQuery(id+"F16.imprint","IMPRINT",FACE,{"disambiguationData":[TD([[makeQuery(id+"F16.imprint","IMPRINT",EDGE,{"derivedFrom":subQ1}),1.0]])]});}
            var Q1;
            {var subQ0=sQuery(id+"F16.wireOp",EDGE,"E85");Q1=makeQuery(id+"F16.imprint","IMPRINT",FACE,{"disambiguationData":[TD([[makeQuery(id+"F16.imprint","IMPRINT",EDGE,{"derivedFrom":subQ0}),-1.0]])]});}
            var Q2;
            {var subQ0=sQuery(id+"F16.wireOp",EDGE,"E93.MirrorCS");Q2=makeQuery(id+"F16.imprint","IMPRINT",FACE,{"disambiguationData":[TD([[makeQuery(id+"F16.imprint","IMPRINT",EDGE,{"derivedFrom":subQ0}),1.0]])]});}
            var Q3;
            Q3=makeQuery(id+"F2.opExtrude","CAP_FACE",FACE,{"disambiguationData":[OSD([sQuery(id+"F0.wireOp",EDGE,"E12"),sQuery(id+"F0.wireOp",EDGE,"E13"),sQuery(id+"F0.wireOp",EDGE,"E14"),sQuery(id+"F0.wireOp",EDGE,"E15"),sQuery(id+"F0.wireOp",EDGE,"E17.filletArc"),sQuery(id+"F0.wireOp",EDGE,"E18.filletArc"),sQuery(id+"F0.wireOp",EDGE,"E19.filletArc"),sQuery(id+"F0.wireOp",EDGE,"E20.filletArc"),sQuery(id+"F0.wireOp",EDGE,"E25.0"),sQuery(id+"F0.wireOp",EDGE,"E25.1"),sQuery(id+"F0.wireOp",EDGE,"E25.2"),sQuery(id+"F0.wireOp",EDGE,"E25.3"),sQuery(id+"F0.wireOp",EDGE,"E25.4"),sQuery(id+"F0.wireOp",EDGE,"E25.5"),sQuery(id+"F0.wireOp",EDGE,"E25.6"),sQuery(id+"F0.wireOp",EDGE,"E25.7")])],"isStart":false});
            extrude(context, id + "F17", {"entities" : qUnion([Q0, Q1, Q2]), "endBound" : BoundingType.UP_TO_SURFACE, "endBoundEntityFace" : qUnion([Q3]), "depth" : 25 * mm});
        }
    });
